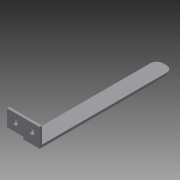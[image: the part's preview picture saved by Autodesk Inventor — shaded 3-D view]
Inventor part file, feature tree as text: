
AUTODESK INVENTOR PART (.ipt)
format: ipt  version: 2015 (Build 190159000, 159)  size: 133,632 bytes
history: native  units: mm
features: sketch x5, extrude x4, other x1, fillet x1, hole x1
ambient origin geometry x8: Origin, YZ Plane, XZ Plane, XY Plane, X Axis, Y Axis, Z Axis, Center Point
bodies: Body1 (feature_tree)
feature tree (12):
  other  "ソリッド1"
  extrude  "押し出し1"  Depth=10.0mm
  fillet  "フィレット1"  Radius=80.0mm
  extrude  "押し出し2"  Depth=1.5mm TaperAngle=0.0deg
  extrude  "押し出し4"  Depth=4.0mm
  extrude  "押し出し5"  Depth=1.5mm TaperAngle=0.0deg
  hole  "穴1"  [1 undecoded]
  sketch  "スケッチ1"
  sketch  "スケッチ2"
  sketch  "スケッチ4"
  sketch  "スケッチ5"
  sketch  "スケッチ7"
note: 1 required parameter value undecoded (feature->parameter linkage not recoverable at this tier; creation-order binding heuristic only, values carry confidence <= 0.55)
